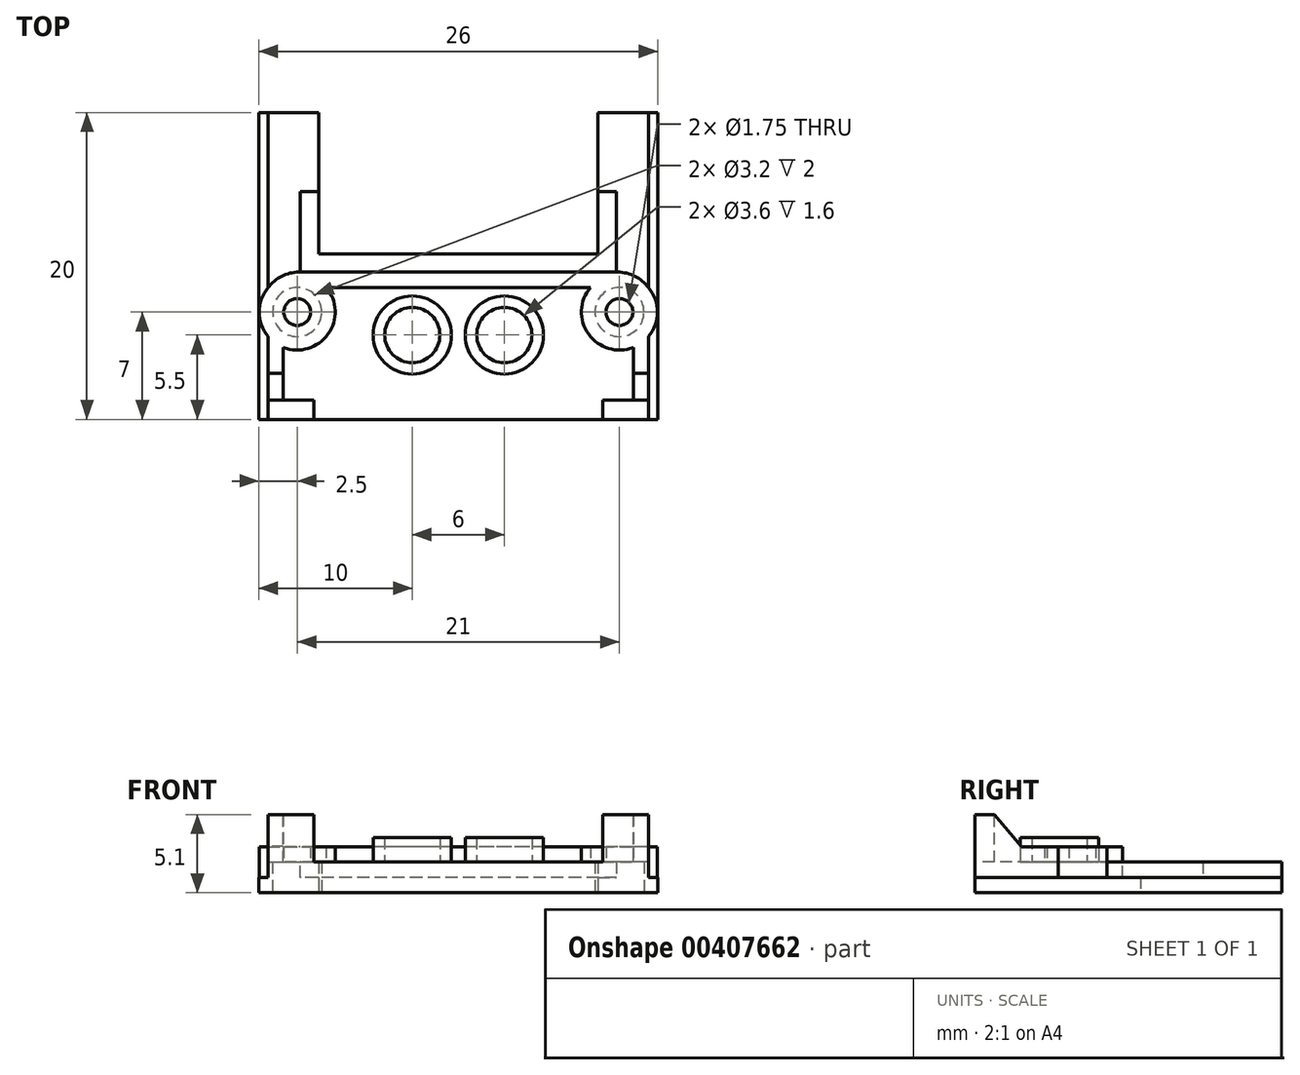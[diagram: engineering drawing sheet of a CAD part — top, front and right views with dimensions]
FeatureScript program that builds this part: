
annotation { "Feature Type Name" : "Feature", "Feature Type Description" : "" }
export const myFeature = defineFeature(function(context is Context, id is Id, definition is map)
    precondition{}
    {
        {
            var Q0;
            Q0=qCreatedBy(makeId("Top.planeOp"),FACE);
            var sketch = newSketch(context, id + "F0", { "sketchPlane" : qUnion([Q0])});
            skCircle(sketch, "E0", {"center": v(10.5, 0) * mm, "radius": 0.87 * mm, "construction": true});
            skLineSegment(sketch, "E1", {"start": v(0, 0) * mm, "end": v(13, 0) * mm, "construction": true});
            skLineSegment(sketch, "E2", {"start": v(13, 0) * mm, "end": v(13, 5.85) * mm, "construction": true});
            skLineSegment(sketch, "E3", {"start": v(0, -7) * mm, "end": v(15.88, -7) * mm, "construction": true});
            skLineSegment(sketch, "E4", {"start": v(-8.49, 13) * mm, "end": v(14.1, 13) * mm, "construction": true});
            skLineSegment(sketch, "E5", {"start": v(-6.44, 3.8) * mm, "end": v(14.47, 3.8) * mm, "construction": true});
            skLineSegment(sketch, "E6", {"start": v(9.1, 10.8) * mm, "end": v(9.1, 2.59) * mm, "construction": true});
            skLineSegment(sketch, "E7", {"start": v(0, 13.76) * mm, "end": v(0, -12.5) * mm, "construction": true});
            skLineSegment(sketch, "E8", {"start": v(0, -7) * mm, "end": v(13, -7) * mm});
            skLineSegment(sketch, "E9", {"start": v(13, -7) * mm, "end": v(13, 13) * mm});
            skLineSegment(sketch, "E10", {"start": v(13, 13) * mm, "end": v(9.1, 13) * mm});
            skLineSegment(sketch, "E11", {"start": v(9.1, 13) * mm, "end": v(9.1, 3.8) * mm});
            skLineSegment(sketch, "E12", {"start": v(9.1, 3.8) * mm, "end": v(0, 3.8) * mm});
            skLineSegment(sketch, "E13", {"start": v(0, 3.8) * mm, "end": v(0, -7) * mm});
            skSolve(sketch);
        }
        {
            var Q0;
            Q0 = qSketchRegion(id + "F0", true);
            extrude(context, id + "F1", {"entities" : qUnion([Q0]), "depth" : 2 * mm});
        }
        {
            var Q0;
            Q0=makeQuery(id+"F1.opExtrude","CAP_FACE",FACE,{"disambiguationData":[OSD([sQuery(id+"F0.wireOp",EDGE,"E8"),sQuery(id+"F0.wireOp",EDGE,"E9"),sQuery(id+"F0.wireOp",EDGE,"E10"),sQuery(id+"F0.wireOp",EDGE,"E11"),sQuery(id+"F0.wireOp",EDGE,"E12"),sQuery(id+"F0.wireOp",EDGE,"E13")])],"isStart":false});
            var sketch = newSketch(context, id + "F2", { "sketchPlane" : qUnion([Q0])});
            skLineSegment(sketch, "E14.bottom", {"start": v(13, -7) * mm, "end": v(12.4, -7) * mm});
            skLineSegment(sketch, "E14.top", {"start": v(13, 13) * mm, "end": v(12.4, 13) * mm});
            skLineSegment(sketch, "E14.left", {"start": v(13, -7) * mm, "end": v(13, 13) * mm});
            skLineSegment(sketch, "E14.right", {"start": v(12.4, -7) * mm, "end": v(12.4, 13) * mm});
            skSolve(sketch);
        }
        {
            var Q0;
            Q0=makeQuery(id+"F2.imprint","IMPRINT",FACE,{"disambiguationData":[TD([[makeQuery(id+"F2.imprint","IMPRINT",EDGE,{"derivedFrom":sQuery(id+"F2.wireOp",EDGE,"E14.bottom")}),1.0]])]});
            extrude(context, id + "F3", {"entities" : qUnion([Q0]), "operationType" : NewBodyOperationType.REMOVE, "oppositeDirection" : true, "depth" : 1 * mm});
        }
        {
            var Q0;
            Q0=makeQuery(id+"F1.opExtrude","CAP_FACE",FACE,{"disambiguationData":[OSD([sQuery(id+"F0.wireOp",EDGE,"E8"),sQuery(id+"F0.wireOp",EDGE,"E9"),sQuery(id+"F0.wireOp",EDGE,"E10"),sQuery(id+"F0.wireOp",EDGE,"E11"),sQuery(id+"F0.wireOp",EDGE,"E12"),sQuery(id+"F0.wireOp",EDGE,"E13")])],"isStart":false});
            var sketch = newSketch(context, id + "F4", { "sketchPlane" : qUnion([Q0])});
            skLineSegment(sketch, "E15", {"start": v(12.4, 2.6) * mm, "end": v(0, 2.6) * mm});
            skLineSegment(sketch, "E16", {"start": v(11.4, -7) * mm, "end": v(12.4, -7) * mm});
            skLineSegment(sketch, "E17", {"start": v(12.4, 2.6) * mm, "end": v(12.4, -7) * mm});
            skLineSegment(sketch, "E18.0", {"start": v(11.4, 1.6) * mm, "end": v(0, 1.6) * mm});
            skLineSegment(sketch, "E19", {"start": v(0, 1.6) * mm, "end": v(0, 2.6) * mm});
            skLineSegment(sketch, "E20", {"start": v(11.4, 1.6) * mm, "end": v(11.4, -7) * mm});
            skSolve(sketch);
        }
        {
            var Q0;
            Q0=makeQuery(id+"F4.imprint","IMPRINT",FACE,{"disambiguationData":[TD([[makeQuery(id+"F4.imprint","IMPRINT",EDGE,{"derivedFrom":sQuery(id+"F4.wireOp",EDGE,"E15")}),1.0]])]});
            extrude(context, id + "F5", {"entities" : qUnion([Q0]), "operationType" : NewBodyOperationType.ADD, "depth" : 1 * mm});
        }
        {
            var Q0;
            {var subQ0=sQuery(id+"F0.wireOp",EDGE,"E13");var subQ1=sQuery(id+"F0.wireOp",EDGE,"E8");Q0=makeQuery(id+"F5.boolean.opBoolean","SPLIT",FACE,{"disambiguationData":[TD([makeQuery(id+"F1.opExtrude","SWEPT_FACE",FACE,{"disambiguationData":[OSD([subQ1])]})])],"derivedFrom":makeQuery(id+"F1.opExtrude","CAP_FACE",FACE,{"disambiguationData":[OSD([subQ1,sQuery(id+"F0.wireOp",EDGE,"E9"),sQuery(id+"F0.wireOp",EDGE,"E10"),sQuery(id+"F0.wireOp",EDGE,"E11"),sQuery(id+"F0.wireOp",EDGE,"E12"),subQ0])],"isStart":false})});}
            var sketch = newSketch(context, id + "F6", { "sketchPlane" : qUnion([Q0])});
            skLineSegment(sketch, "E21.bottom", {"start": v(9.4, -5.75) * mm, "end": v(12.4, -5.75) * mm});
            skLineSegment(sketch, "E21.top", {"start": v(9.4, -7) * mm, "end": v(12.4, -7) * mm});
            skLineSegment(sketch, "E21.left", {"start": v(9.4, -5.75) * mm, "end": v(9.4, -7) * mm});
            skLineSegment(sketch, "E21.right", {"start": v(12.4, -5.75) * mm, "end": v(12.4, -7) * mm});
            skSolve(sketch);
        }
        {
            var Q0;
            Q0 = qSketchRegion(id + "F6", true);
            extrude(context, id + "F7", {"entities" : qUnion([Q0]), "operationType" : NewBodyOperationType.ADD, "depth" : 3.1 * mm});
        }
        {
            var Q0;
            Q0=makeQuery(id+"F5.opExtrude","CAP_FACE",FACE,{"disambiguationData":[OSD([sQuery(id+"F4.wireOp",EDGE,"BoG8ja5q-0o1P-bq9L-j6nZ-SlOVDtmsTbaq"),sQuery(id+"F4.wireOp",EDGE,"E15"),sQuery(id+"F4.wireOp",EDGE,"E16"),sQuery(id+"F4.wireOp",EDGE,"MYOL4ilY-3U7f-L9R3-0GRE-ep05zuKfo2ip"),sQuery(id+"F4.wireOp",EDGE,"Std8EdV7-EM8q-YtSH-xnsP-5hMkUNyJZBRs"),sQuery(id+"F4.wireOp",EDGE,"E17")])],"isStart":false});
            var sketch = newSketch(context, id + "F8", { "sketchPlane" : qUnion([Q0])});
            skLineSegment(sketch, "E22.bottom", {"start": v(12.4, -5.75) * mm, "end": v(11.4, -5.75) * mm});
            skLineSegment(sketch, "E22.top", {"start": v(12.4, -4) * mm, "end": v(11.4, -4) * mm});
            skLineSegment(sketch, "E22.left", {"start": v(12.4, -5.75) * mm, "end": v(12.4, -4) * mm});
            skLineSegment(sketch, "E22.right", {"start": v(11.4, -5.75) * mm, "end": v(11.4, -4) * mm});
            skSolve(sketch);
        }
        {
            var Q0;
            Q0 = qSketchRegion(id + "F8", true);
            extrude(context, id + "F9", {"entities" : qUnion([Q0]), "operationType" : NewBodyOperationType.ADD, "depth" : 2.1 * mm});
        }
        {
            var Q0;
            Q0=makeQuery(id+"F9.opExtrude","CAP_EDGE",EDGE,{"disambiguationData":[OSD([sQuery(id+"F8.wireOp",EDGE,"E22.top")])],"isStart":false});
            chamfer(context, id + "F10", {"entities" : qUnion([Q0]), "chamferType" : ChamferType.OFFSET_ANGLE, "width" : 1.75 * mm, "oppositeDirection" : false, "angle" : 50 * degree, "tangentPropagation" : true});
        }
        {
            var Q0;
            Q0=qCreatedBy(makeId("Top.planeOp"),FACE);
            var sketch = newSketch(context, id + "F11", { "sketchPlane" : qUnion([Q0])});
            skCircle(sketch, "E23.0", {"center": v(10.5, 0) * mm, "radius": 0.87 * mm});
            skCircle(sketch, "E24.0", {"center": v(10.5, 0) * mm, "radius": 2.47 * mm});
            skSolve(sketch);
        }
        {
            var Q0;
            Q0 = qSketchRegion(id + "F11", true);
            extrude(context, id + "F12", {"entities" : qUnion([Q0]), "operationType" : NewBodyOperationType.ADD, "depth" : 3 * mm});
        }
        {
            var Q0;
            Q0=makeQuery(id+"F5.opExtrude","SWEPT_EDGE",EDGE,{"disambiguationData":[OSD([sQuery(id+"F2.wireOp",EDGE,"E14.right"),sQuery(id+"F4.wireOp",EDGE,"E15"),sQuery(id+"F4.wireOp",EDGE,"E17")])]});
            fillet(context, id + "F13", {"entities" : qUnion([Q0]), "radius" : 2.5 * mm, "tangentPropagation" : true, "allowEdgeOverflow" : false});
        }
        {
            var Q0;
            Q0=makeQuery(id+"F0.imprint","IMPRINT",FACE,{"disambiguationData":[TD([[makeQuery(id+"F0.imprint","IMPRINT",EDGE,{"derivedFrom":sQuery(id+"F0.wireOp",EDGE,"E8")}),1.0]])]});
            var sketch = newSketch(context, id + "F14", { "sketchPlane" : qUnion([Q0])});
            skCircle(sketch, "E25.0", {"center": v(10.5, 0) * mm, "radius": 0.87 * mm});
            skSolve(sketch);
        }
        {
            var Q0;
            Q0 = qSketchRegion(id + "F14", true);
            extrude(context, id + "F15", {"entities" : qUnion([Q0]), "operationType" : NewBodyOperationType.REMOVE, "endBound" : BoundingType.THROUGH_ALL, "depth" : 25 * mm});
        }
        {
            var Q0;
            {var subQ0=sQuery(id+"F0.wireOp",EDGE,"E13");var subQ1=sQuery(id+"F0.wireOp",EDGE,"E12");var subQ2=sQuery(id+"F0.wireOp",EDGE,"E11");var subQ3=sQuery(id+"F0.wireOp",EDGE,"E10");Q0=makeQuery(id+"F5.boolean.opBoolean","SPLIT",FACE,{"disambiguationData":[TD([makeQuery(id+"F1.opExtrude","SWEPT_FACE",FACE,{"disambiguationData":[OSD([subQ3])]})])],"derivedFrom":makeQuery(id+"F1.opExtrude","CAP_FACE",FACE,{"disambiguationData":[OSD([sQuery(id+"F0.wireOp",EDGE,"E8"),sQuery(id+"F0.wireOp",EDGE,"E9"),subQ3,subQ2,subQ1,subQ0])],"isStart":false})});}
            var sketch = newSketch(context, id + "F16", { "sketchPlane" : qUnion([Q0])});
            skLineSegment(sketch, "E26.0", {"start": v(9.1, 13) * mm, "end": v(9.1, 3.8) * mm});
            skLineSegment(sketch, "E27.0", {"start": v(9.1, 3.8) * mm, "end": v(0, 3.8) * mm});
            skLineSegment(sketch, "E28.0", {"start": v(10.3, 2.6) * mm, "end": v(0, 2.6) * mm});
            skLineSegment(sketch, "E28.1", {"start": v(10.3, 13) * mm, "end": v(10.3, 2.6) * mm});
            skLineSegment(sketch, "E29", {"start": v(0, 2.6) * mm, "end": v(0, 3.8) * mm});
            skLineSegment(sketch, "E30", {"start": v(10.3, 13) * mm, "end": v(9.1, 13) * mm});
            skSolve(sketch);
        }
        {
            var Q0;
            Q0=makeQuery(id+"F16.imprint","IMPRINT",FACE,{"disambiguationData":[TD([[makeQuery(id+"F16.imprint","IMPRINT",EDGE,{"derivedFrom":sQuery(id+"F16.wireOp",EDGE,"E26.0")}),1.0]])]});
            extrude(context, id + "F17", {"entities" : qUnion([Q0]), "operationType" : NewBodyOperationType.REMOVE, "oppositeDirection" : true, "depth" : 1 * mm});
        }
        {
            var Q0;
            Q0=makeQuery(id+"F17.boolean.opBoolean","COPY",FACE,{"derivedFrom":makeQuery(id+"F17.opExtrude","SWEPT_FACE",FACE,{"disambiguationData":[OSD([sQuery(id+"F16.wireOp",EDGE,"E28.1")])]})});
            var sketch = newSketch(context, id + "F18", { "sketchPlane" : qUnion([Q0])});
            skLineSegment(sketch, "E31.bottom", {"start": v(-13, 2) * mm, "end": v(-7.85, 2) * mm});
            skLineSegment(sketch, "E31.top", {"start": v(-13, 1) * mm, "end": v(-7.85, 1) * mm});
            skLineSegment(sketch, "E31.left", {"start": v(-13, 2) * mm, "end": v(-13, 1) * mm});
            skLineSegment(sketch, "E31.right", {"start": v(-7.85, 2) * mm, "end": v(-7.85, 1) * mm});
            skSolve(sketch);
        }
        {
            var Q0;
            Q0=makeQuery(id+"F18.imprint","IMPRINT",FACE,{"disambiguationData":[TD([[makeQuery(id+"F18.imprint","IMPRINT",EDGE,{"derivedFrom":sQuery(id+"F18.wireOp",EDGE,"E31.bottom")}),-1.0]])]});
            extrude(context, id + "F19", {"entities" : qUnion([Q0]), "operationType" : NewBodyOperationType.ADD, "depth" : 1.2 * mm});
        }
        {
            var Q0;
            Q0=makeQuery(id+"F0.imprint","IMPRINT",FACE,{"disambiguationData":[TD([[makeQuery(id+"F0.imprint","IMPRINT",EDGE,{"derivedFrom":sQuery(id+"F0.wireOp",EDGE,"E8")}),1.0]])]});
            var sketch = newSketch(context, id + "F20", { "sketchPlane" : qUnion([Q0])});
            skCircle(sketch, "E32.0", {"center": v(10.5, 0) * mm, "radius": 0.87 * mm, "construction": true});
            skCircle(sketch, "E33", {"center": v(10.5, 0) * mm, "radius": 1.6 * mm});
            skSolve(sketch);
        }
        {
            var Q0;
            Q0 = qSketchRegion(id + "F20", true);
            extrude(context, id + "F21", {"entities" : qUnion([Q0]), "operationType" : NewBodyOperationType.REMOVE, "depth" : 2 * mm});
        }
        {
            var Q0;
            {var subQ2=sQuery(id+"F0.wireOp",EDGE,"E8");var subQ3=makeQuery(id+"F1.opExtrude","SWEPT_FACE",FACE,{"disambiguationData":[OSD([subQ2])]});var subQ5=sQuery(id+"F0.wireOp",EDGE,"E13");Q0=makeQuery(id+"F12.boolean.opBoolean","SPLIT",FACE,{"disambiguationData":[TD([subQ3])],"derivedFrom":makeQuery(id+"F5.boolean.opBoolean","SPLIT",FACE,{"disambiguationData":[TD([subQ3])],"derivedFrom":makeQuery(id+"F1.opExtrude","CAP_FACE",FACE,{"disambiguationData":[OSD([subQ2,sQuery(id+"F0.wireOp",EDGE,"E9"),sQuery(id+"F0.wireOp",EDGE,"E10"),sQuery(id+"F0.wireOp",EDGE,"E11"),sQuery(id+"F0.wireOp",EDGE,"E12"),subQ5])],"isStart":false})})});}
            var sketch = newSketch(context, id + "F22", { "sketchPlane" : qUnion([Q0])});
            skCircle(sketch, "E34.0", {"center": v(10.5, 0) * mm, "radius": 0.87 * mm, "construction": true});
            skLineSegment(sketch, "E35", {"start": v(3, 4.95) * mm, "end": v(3, -9.4) * mm, "construction": true});
            skLineSegment(sketch, "E36", {"start": v(0, -1.5) * mm, "end": v(17.15, -1.5) * mm, "construction": true});
            skCircle(sketch, "E37", {"center": v(3, -1.5) * mm, "radius": 1.8 * mm});
            skCircle(sketch, "E38", {"center": v(3, -1.5) * mm, "radius": 2.55 * mm});
            skSolve(sketch);
        }
        {
            var Q0;
            Q0 = qSketchRegion(id + "F22", true);
            extrude(context, id + "F23", {"entities" : qUnion([Q0]), "operationType" : NewBodyOperationType.ADD, "depth" : 1.6 * mm});
        }
        {
            var Q0;
            Q0=makeQuery(id+"F1.opExtrude","SWEPT_BODY",BODY,{"disambiguationData":[OSD([sQuery(id+"F0.wireOp",EDGE,"E8"),sQuery(id+"F0.wireOp",EDGE,"E9"),sQuery(id+"F0.wireOp",EDGE,"E10"),sQuery(id+"F0.wireOp",EDGE,"E11"),sQuery(id+"F0.wireOp",EDGE,"E12"),sQuery(id+"F0.wireOp",EDGE,"E13")])]});
            var Q1;
            Q1=makeQuery(id+"F5.boolean.opBoolean","MERGE",FACE,{"derivedFrom":[makeQuery(id+"F1.opExtrude","SWEPT_FACE",FACE,{"disambiguationData":[OSD([sQuery(id+"F0.wireOp",EDGE,"E13")])]}),makeQuery(id+"F5.opExtrude","SWEPT_FACE",FACE,{"disambiguationData":[OSD([sQuery(id+"F4.wireOp",EDGE,"E19")])]})]});
            mirror(context, id + "F24", {"operationType" : NewBodyOperationType.ADD, "entities" : qUnion([Q0]), "mirrorPlane" : qUnion([Q1])});
        }
    });
